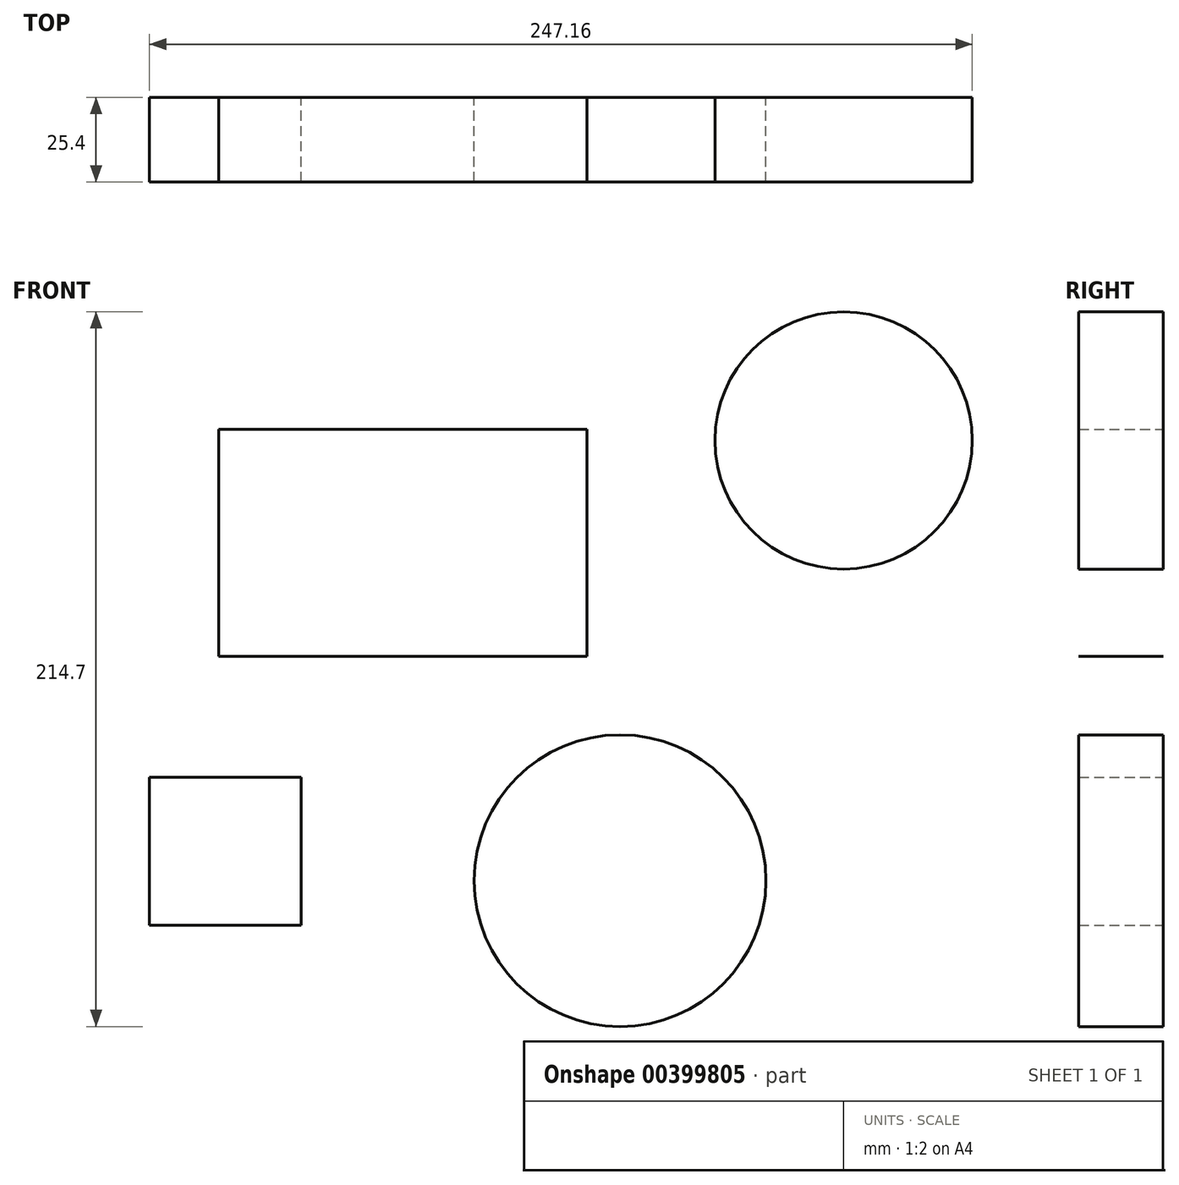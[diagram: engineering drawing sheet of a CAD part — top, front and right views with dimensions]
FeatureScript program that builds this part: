
annotation { "Feature Type Name" : "Feature", "Feature Type Description" : "" }
export const myFeature = defineFeature(function(context is Context, id is Id, definition is map)
    precondition{}
    {
        {
            var Q0;
            Q0=qCreatedBy(makeId("Front.planeOp"),FACE);
            var sketch = newSketch(context, id + "F0", { "sketchPlane" : qUnion([Q0])});
            skLineSegment(sketch, "E0.bottom", {"start": v(-97.9, 41.11) * mm, "end": v(12.72, 41.11) * mm});
            skLineSegment(sketch, "E0.top", {"start": v(-97.9, -27.1) * mm, "end": v(12.72, -27.1) * mm});
            skLineSegment(sketch, "E0.left", {"start": v(-97.9, 41.11) * mm, "end": v(-97.9, -27.1) * mm});
            skLineSegment(sketch, "E0.right", {"start": v(12.72, 41.11) * mm, "end": v(12.72, -27.1) * mm});
            skCircle(sketch, "E1", {"center": v(89.78, 37.8) * mm, "radius": 38.64 * mm});
            skLineSegment(sketch, "E2.bottom", {"start": v(-118.73, -63.44) * mm, "end": v(-73.16, -63.44) * mm});
            skLineSegment(sketch, "E2.top", {"start": v(-118.73, -107.78) * mm, "end": v(-73.16, -107.78) * mm});
            skLineSegment(sketch, "E2.left", {"start": v(-118.73, -63.44) * mm, "end": v(-118.73, -107.78) * mm});
            skLineSegment(sketch, "E2.right", {"start": v(-73.16, -63.44) * mm, "end": v(-73.16, -107.78) * mm});
            skCircle(sketch, "E3", {"center": v(22.65, -94.45) * mm, "radius": 43.81 * mm});
            skSolve(sketch);
        }
        {
            var Q0;
            Q0 = qSketchRegion(id + "F0", true);
            extrude(context, id + "F1", {"entities" : qUnion([Q0]), "depth" : 25.4 * mm});
        }
    });
